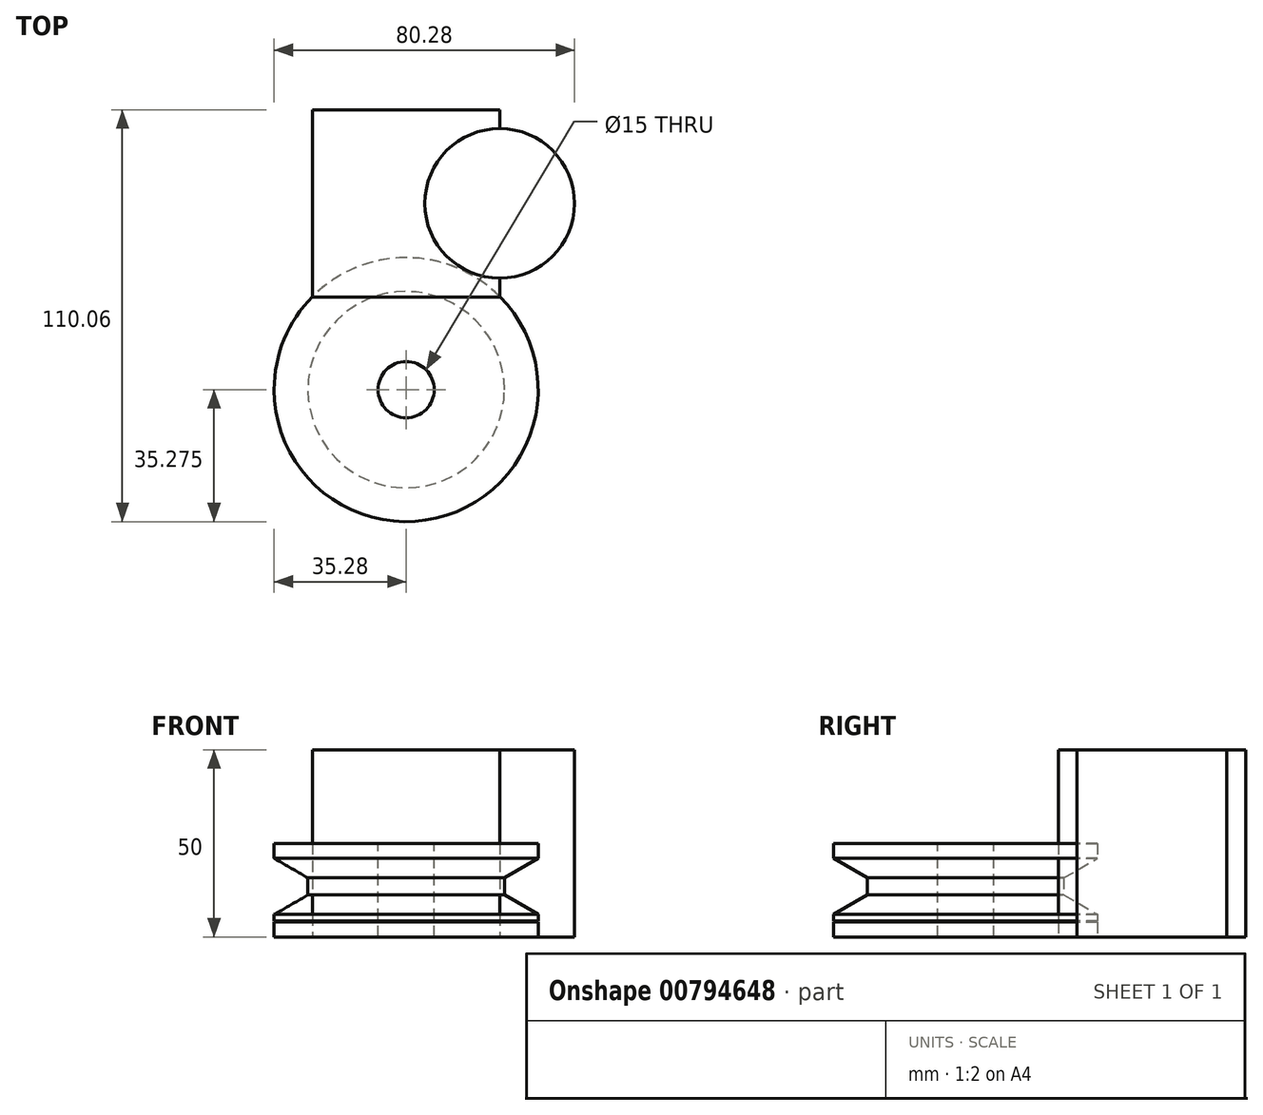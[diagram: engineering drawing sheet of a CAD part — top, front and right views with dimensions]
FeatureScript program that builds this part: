
annotation { "Feature Type Name" : "Feature", "Feature Type Description" : "" }
export const myFeature = defineFeature(function(context is Context, id is Id, definition is map)
    precondition{}
    {
        {
            var Q0;
            Q0=qCreatedBy(makeId("Top.planeOp"),FACE);
            var sketch = newSketch(context, id + "F0", { "sketchPlane" : qUnion([Q0])});
            skLineSegment(sketch, "E0.bottom", {"start": v(-25, 25) * mm, "end": v(25, 25) * mm});
            skLineSegment(sketch, "E0.top", {"start": v(-25, -25) * mm, "end": v(25, -25) * mm});
            skLineSegment(sketch, "E0.left", {"start": v(-25, 25) * mm, "end": v(-25, -25) * mm});
            skLineSegment(sketch, "E0.right", {"start": v(25, 25) * mm, "end": v(25, -25) * mm});
            skPoint(sketch, "E0.middle", {"position": v(0, 0) * mm});
            skCircle(sketch, "E1", {"center": v(25, 0) * mm, "radius": 20 * mm});
            skSolve(sketch);
        }
        {
            var Q0;
            Q0=makeQuery(id+"F0.imprint","IMPRINT",FACE,{"disambiguationData":[TD([[makeQuery(id+"F0.imprint","IMPRINT",EDGE,{"derivedFrom":sQuery(id+"F0.wireOp",EDGE,"E0.bottom")}),-1.0]])]});
            extrude(context, id + "F1", {"entities" : qUnion([Q0]), "depth" : 50 * mm, "offsetDistance" : 25 * mm});
        }
        {
            var Q0;
            Q0=makeQuery(id+"F0.imprint","IMPRINT",FACE,{"disambiguationData":[TD([[makeQuery(id+"F0.imprint","IMPRINT",EDGE,{"derivedFrom":sQuery(id+"F0.wireOp",EDGE,"E1")}),1.0]])]});
            extrude(context, id + "F2", {"entities" : qUnion([Q0]), "depth" : 50 * mm, "offsetDistance" : 25 * mm});
        }
        {
            var Q0;
            Q0=qCreatedBy(makeId("Right.planeOp"),FACE);
            var sketch = newSketch(context, id + "F3", { "sketchPlane" : qUnion([Q0])});
            skLineSegment(sketch, "E2.bottom", {"start": v(-14.5, 0) * mm, "end": v(-49.79, 0) * mm});
            skLineSegment(sketch, "E2.top", {"start": v(-14.5, 25) * mm, "end": v(-49.79, 25) * mm});
            skLineSegment(sketch, "E2.right", {"start": v(-49.79, 0) * mm, "end": v(-49.79, 25) * mm});
            skLineSegment(sketch, "E3", {"start": v(-14.5, 25) * mm, "end": v(-14.5, 21) * mm});
            skLineSegment(sketch, "E4", {"start": v(-14.5, 21) * mm, "end": v(-23.55, 15.78) * mm});
            skLineSegment(sketch, "E5", {"start": v(-23.55, 15.78) * mm, "end": v(-23.55, 11.2) * mm});
            skLineSegment(sketch, "E6", {"start": v(-23.55, 11.2) * mm, "end": v(-14.5, 5.99) * mm});
            skLineSegment(sketch, "E7", {"start": v(-14.5, 5.99) * mm, "end": v(-14.5, 4.33) * mm});
            skLineSegment(sketch, "E8", {"start": v(-14.5, 4.33) * mm, "end": v(-23.55, 4.33) * mm});
            skLineSegment(sketch, "E9", {"start": v(-23.55, 4.33) * mm, "end": v(-23.55, 4) * mm});
            skLineSegment(sketch, "E10", {"start": v(-23.55, 4) * mm, "end": v(-14.5, 4) * mm});
            skLineSegment(sketch, "E11", {"start": v(-14.5, 4) * mm, "end": v(-14.5, 0) * mm});
            skSolve(sketch);
        }
        {
            var Q0;
            Q0=makeQuery(id+"F3.imprint","IMPRINT",FACE,{"disambiguationData":[TD([[makeQuery(id+"F3.imprint","IMPRINT",EDGE,{"derivedFrom":sQuery(id+"F3.wireOp",EDGE,"E2.bottom")}),-1.0]])]});
            var Q1;
            Q1=sQuery(id+"F3.wireOp",EDGE,"E2.right");
            revolve(context, id + "F4", {"surfaceOperationType" : NewSurfaceOperationType.NEW, "entities" : qUnion([Q0]), "axis" : qUnion([Q1]), "revolveType" : RevolveType.FULL});
        }
        {
            var Q0;
            Q0=makeQuery(id+"F4.opRevolve","SWEPT_FACE",FACE,{"disambiguationData":[OSD([sQuery(id+"F3.wireOp",EDGE,"E2.top")])]});
            var sketch = newSketch(context, id + "F5", { "sketchPlane" : qUnion([Q0])});
            skCircle(sketch, "E12", {"center": v(0, -49.79) * mm, "radius": 7.5 * mm});
            skSolve(sketch);
        }
        {
            var Q0;
            Q0=makeQuery(id+"F5.imprint","IMPRINT",FACE,{"disambiguationData":[TD([[makeQuery(id+"F5.imprint","IMPRINT",EDGE,{"derivedFrom":sQuery(id+"F5.wireOp",EDGE,"E12")}),1.0]])]});
            extrude(context, id + "F6", {"entities" : qUnion([Q0]), "operationType" : NewBodyOperationType.REMOVE, "endBound" : BoundingType.THROUGH_ALL, "oppositeDirection" : true, "depth" : 48.9 * mm, "offsetDistance" : 25 * mm});
        }
    });
